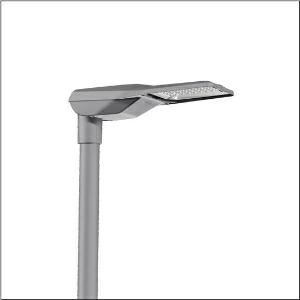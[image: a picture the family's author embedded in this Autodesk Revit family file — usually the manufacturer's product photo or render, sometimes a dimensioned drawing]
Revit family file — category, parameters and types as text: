
# Revit family: streetlight_sl_21_iq_mini___st1_0a_5xe2d31g08jb_707a
name_source: partatom
category: Lighting Fixtures
units: mm (PartAtom-declared; Revit-internal decimal feet)

## family parameters
Cut with Voids When Loaded = No
Host = Face
Light Source = No
Part Type = Normal
Room Calculation Point = No
Round Connector Dimension = Use Diameter
Shared = No

## types (1)
- --- (1 x LED, 10820 lm, 71.6 W, 3000K)
    Apparent Load = 72 VA
    CIE Flux Codes = 40 73 97 100 100
    Color Rendering = 70
    Color Temperature = 3000K
    Default Elevation = 1800 mm
    Description = Streetlight SL 21 iQ mini, mast luminaire, primary light control with lens, of PMMA, primary optical cover: cover, of toughened safety glass, transparent, light distribution: ST1.0a, light emission: direct distribution, primary light characteristic: asymmetric, installation type: post-top, side-entry, LED, High Power LED, rated luminous flux: 10.820lm, luminous efficacy: 151lm/W, light colour: 730, colour temperature: 3000K, control: Street-Remote, Auto-Match, Temp-Guard, Lumen-Switch, Night-Set, Smart-Wire, Light-Fading, Desk-Remote (wireless, voltage-free reading and setting of iQ features in the workshop via application-optimized NFC function/RFID function), optimised constant luminous flux control (CLO 2.0), presetting dimming linear, mains connection: 220..240V, AC, 50/60Hz, start of lifetime: 72W, end of service life: 75W, reduction: 33W, luminaire housing, of diecast aluminium, powder-coated, Siteco® metallic grey (DB 702S), corrosivity category C5 mid according to DIN EN ISO 12944, please order mast flange separately, inclination adjustable: 0°, 5°, 10°, 15°, sealing non-destructively replaceable, multi-level sealing system, length: 628mm, width: 235mm, height: 110mm, mast flange for spigot size: 42mm (side-entry): 5XC10008XM4, 60/48mm (side-entry/post-top): 5XC10108XM2, 76/60mm (side-entry/post-top): 5XC10108XM1, protection rating (complete): IP66, insulation class (complete): insulation class II (safety insulation), certification: CE, ENEC, ENEC+, VDE, impact resistance: IK09, permissible operating ambient temperature for outdoor applications: -40..+50°C, standard-compliant lighting for roads and squares, packaging unit: 1 piece

Light Distribution: ST1.0a
    Height = 110 mm
    Lamp = 1 x LED
    Lamp Light Flux = 10820 lm
    Lamp Power = 71.6 W
    Lamp count = 1
    Length = 625 mm
    Luminous efficacy = 151 lm/W
    Manufacturer = Siteco
    ModVariant = No
    Model = 5XE2D31G08JB
    Number of Poles = 1
    OnlyDefault = Yes
    Power Factor = 1
    Product Name = Streetlight SL 21 iQ mini | ST1.0a
    Product group = mast luminaire | pylon top
    ProductGroupID = 6100
    Protection Class = Protection class II
    Protection Degree = IP 66
    RLX_Detail_Level = 1
    RLX_Emergency_Light_Flux = 0 lm
    RLX_Emergency_Type = 0
    RLX_Emergency_Type_DB = No
    RlxData = <blob elided: 92117 chars, md5=fae58378>
    Socket = socket
    Standby Power = 0 W
    System Light Flux = 10820 lm
    System Power = 72 W
    Type Comments = factory setting: luminous flux: 100 % | dim-lin: 254 | 746 mA
    Type Image = l_1003519.jpg
    URL = http://relux.com
    VarID = @adj_104085
    Voltage = 0 V
    Weight = 0.00 kg
    Width = 234 mm

## geometry (parser evidence)
native form markers: Blend x4, Sweep x11
no freeform markers — native parametric forms only
